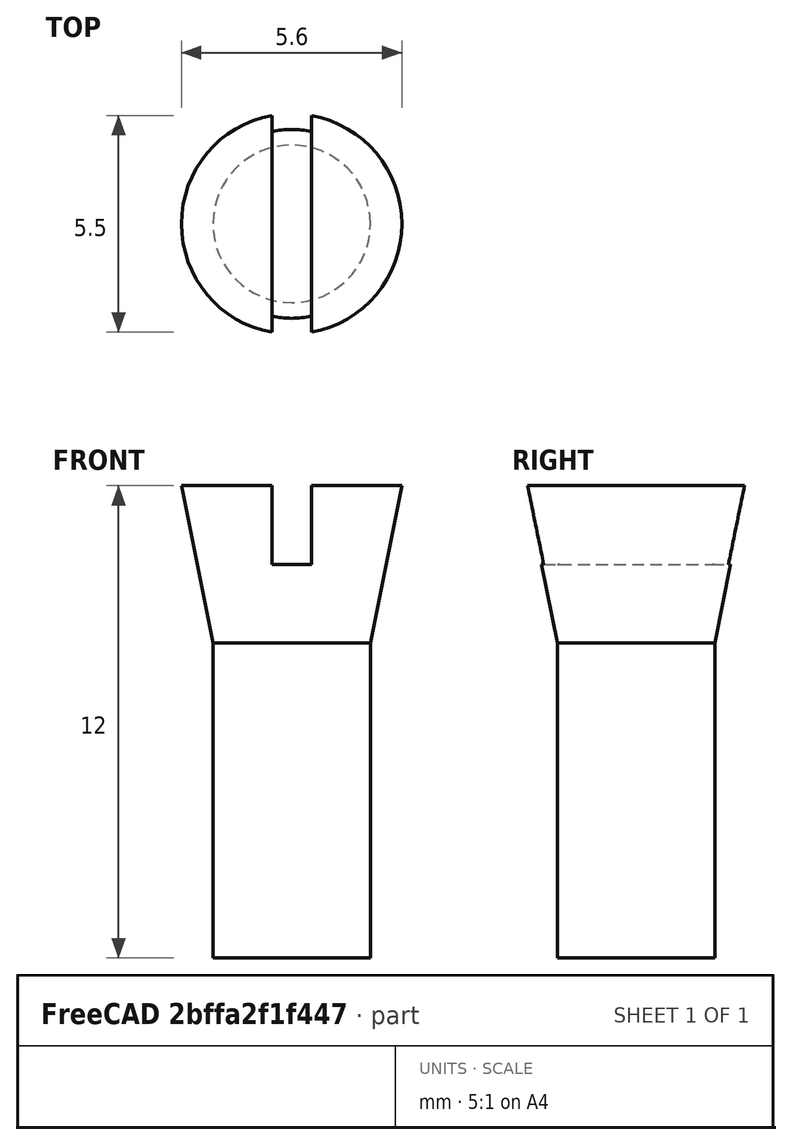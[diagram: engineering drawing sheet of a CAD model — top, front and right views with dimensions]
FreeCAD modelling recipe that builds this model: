
FCSTD DOCUMENT  (FreeCAD 0.20R29177 (Git))
Label: EjercicioVideo14
License: All rights reserved
LicenseURL: http://en.wikipedia.org/wiki/All_rights_reserved
objects: Part::Cylinder×1, Part::Cone×1, Part::Box×1, Part::Cut×1, Part::Fuse×1
note: 5 computed .brp shape members not serialized (recipe doc carries the construction recipe); baked Part::Feature solids carry a one-line shape summary decoded from their .brp

FEATURE [Part::Cylinder] Cylinder  label="Cilindro"
  Angle = 360
  AttacherType = Attacher::AttachEngine3D
  FirstAngle = 0
  Height = 10
  Radius = 2
  SecondAngle = 0
FEATURE [Part::Cone] Cone  label="Cono"
  Angle = 360
  AttacherType = Attacher::AttachEngine3D
  Height = 4
  Placement = pos=(0,0,8) rot=(0,0,1;0rad)
  Radius1 = 2
  Radius2 = 2.8
FEATURE [Part::Box] Box  label="Cubo"
  AttacherType = Attacher::AttachEngine3D
  Height = 2
  Length = 1
  Placement = pos=(-0.5,-5,10) rot=(0,0,1;0rad)
  Width = 10
FEATURE [Part::Cut] Cut
  Base = -> Cone
  Tool = -> Box
FEATURE [Part::Fuse] Fusion
  Base = -> Cylinder
  Tool = -> Cut
